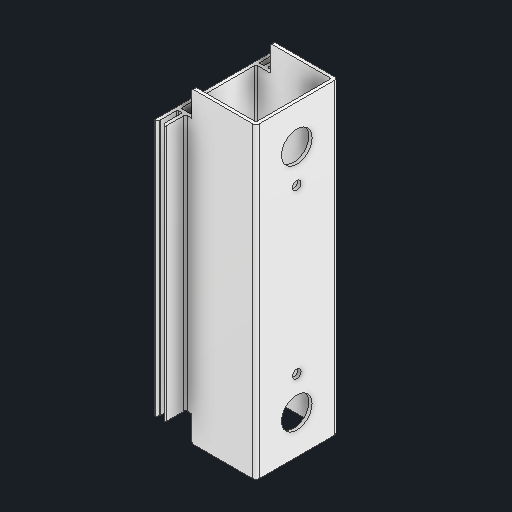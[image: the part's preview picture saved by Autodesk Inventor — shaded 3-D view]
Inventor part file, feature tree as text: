
AUTODESK INVENTOR PART (.ipt)
format: ipt  version: 2024.2 (Build 282272000, 272)  size: 144,384 bytes
history: native  units: in
note: dims shown in document units (in); Inventor stores cm internally (conversion verified against a paired STEP export)
features: fillet x1
ambient origin geometry x8: Origin, YZ Plane, XZ Plane, XY Plane, X Axis, Y Axis, Z Axis, Center Point
bodies: Solid1 (feature_tree)
feature tree (1):
  fillet  "Fillet7"  [1 undecoded]
note: 1 required parameter value undecoded (feature->parameter linkage not recoverable at this tier; creation-order binding heuristic only, values carry confidence <= 0.55)
